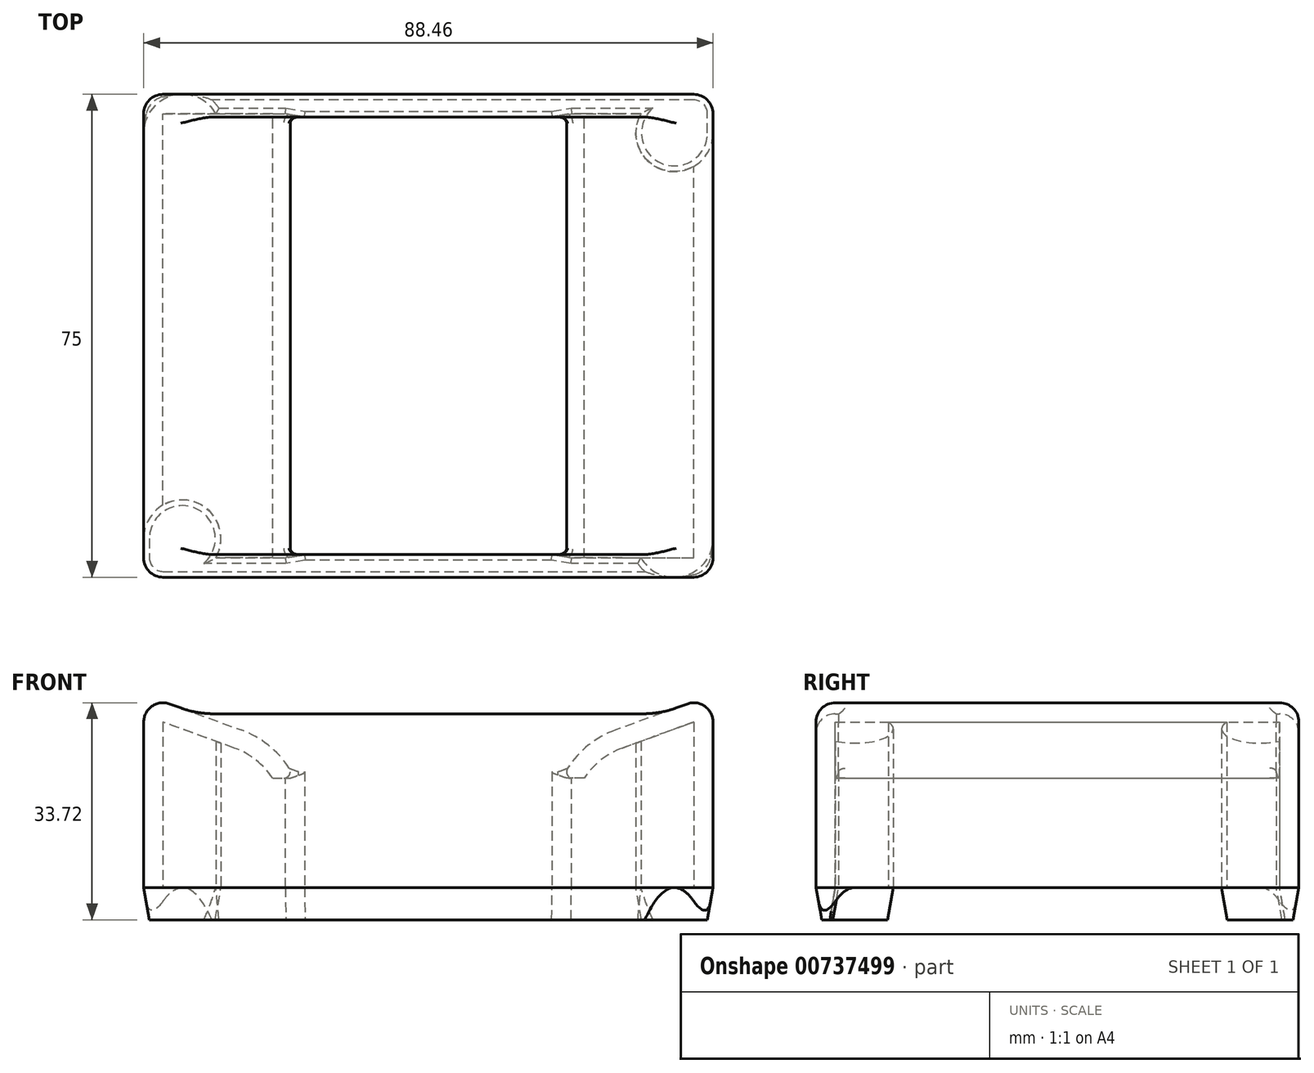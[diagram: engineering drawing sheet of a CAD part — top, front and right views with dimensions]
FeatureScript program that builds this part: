
annotation { "Feature Type Name" : "Feature", "Feature Type Description" : "" }
export const myFeature = defineFeature(function(context is Context, id is Id, definition is map)
    precondition{}
    {
        {
            var Q0;
            Q0=qCreatedBy(makeId("Front.planeOp"),FACE);
            var sketch = newSketch(context, id + "F0", { "sketchPlane" : qUnion([Q0])});
            skCircle(sketch, "E0", {"center": v(0, 115) * mm, "radius": 95 * mm, "construction": true});
            skPoint(sketch, "E1.middle", {"position": v(0, 0) * mm});
            skLineSegment(sketch, "E2", {"start": v(-44.23, 0) * mm, "end": v(44.23, 0) * mm});
            skLineSegment(sketch, "E3", {"start": v(-19.23, 20.9) * mm, "end": v(-19.23, 0) * mm});
            skLineSegment(sketch, "E4", {"start": v(-44.23, 30) * mm, "end": v(-19.23, 20.9) * mm});
            skLineSegment(sketch, "E5", {"start": v(-44.23, 30) * mm, "end": v(-44.23, 0) * mm});
            skLineSegment(sketch, "E6.MirrorCS", {"start": v(44.23, 30) * mm, "end": v(44.23, 0) * mm});
            skLineSegment(sketch, "E7.MirrorCS", {"start": v(19.23, 20.9) * mm, "end": v(19.23, 0) * mm});
            skLineSegment(sketch, "E8.MirrorCS", {"start": v(44.23, 30) * mm, "end": v(19.23, 20.9) * mm});
            skLineSegment(sketch, "E9", {"start": v(-35.98, 27) * mm, "end": v(35.98, 27) * mm});
            skSolve(sketch);
        }
        {
            var Q0;
            {var subQ3=sQuery(id+"F0.wireOp",EDGE,"E3");Q0=makeQuery(id+"F0.imprint","IMPRINT",FACE,{"disambiguationData":[TD([[makeQuery(id+"F0.imprint","IMPRINT",EDGE,{"derivedFrom":subQ3}),-1.0]])]});}
            var Q1;
            {var subQ1=sQuery(id+"F0.wireOp",EDGE,"E3");Q1=makeQuery(id+"F0.imprint","IMPRINT",FACE,{"disambiguationData":[TD([[makeQuery(id+"F0.imprint","IMPRINT",EDGE,{"derivedFrom":subQ1}),1.0]])]});}
            var Q2;
            {var subQ1=sQuery(id+"F0.wireOp",EDGE,"E6.MirrorCS");Q2=makeQuery(id+"F0.imprint","IMPRINT",FACE,{"disambiguationData":[TD([[makeQuery(id+"F0.imprint","IMPRINT",EDGE,{"derivedFrom":subQ1}),-1.0]])]});}
            extrude(context, id + "F1", {"entities" : qUnion([Q0, Q1, Q2]), "endBound" : BoundingType.SYMMETRIC, "depth" : 75 * mm, "offsetDistance" : 25 * mm});
        }
        {
            var Q0;
            {var subQ1=sQuery(id+"F0.wireOp",EDGE,"E3");Q0=makeQuery(id+"F0.imprint","IMPRINT",FACE,{"disambiguationData":[TD([[makeQuery(id+"F0.imprint","IMPRINT",EDGE,{"derivedFrom":subQ1}),1.0]])]});}
            extrude(context, id + "F2", {"entities" : qUnion([Q0]), "operationType" : NewBodyOperationType.REMOVE, "endBound" : BoundingType.SYMMETRIC, "depth" : 68 * mm, "offsetDistance" : 25 * mm});
        }
        {
            var Q0;
            Q0=makeQuery(id+"F2.boolean.opBoolean","COPY",EDGE,{"derivedFrom":makeQuery(id+"F2.opExtrude","SWEPT_EDGE",EDGE,{"disambiguationData":[OSD([sQuery(id+"F0.wireOp",EDGE,"E3"),sQuery(id+"F0.wireOp",EDGE,"E4")])]})});
            var Q1;
            Q1=makeQuery(id+"F2.boolean.opBoolean","COPY",EDGE,{"derivedFrom":makeQuery(id+"F2.opExtrude","SWEPT_EDGE",EDGE,{"disambiguationData":[OSD([sQuery(id+"F0.wireOp",EDGE,"E7.MirrorCS"),sQuery(id+"F0.wireOp",EDGE,"E8.MirrorCS")])]})});
            var Q2;
            {var subQ0=sQuery(id+"F0.wireOp",EDGE,"E9");var subQ1=sQuery(id+"F0.wireOp",EDGE,"E8.MirrorCS");var subQ2=sQuery(id+"F0.wireOp",EDGE,"E4");var subQ3=sQuery(id+"F0.wireOp",EDGE,"E2");Q2=makeQuery(id+"F2.boolean.opBoolean","SPLIT",EDGE,{"disambiguationData":[TD([makeQuery(id+"F1.opExtrude","CAP_FACE",FACE,{"disambiguationData":[OSD([subQ3,subQ2,sQuery(id+"F0.wireOp",EDGE,"E5"),sQuery(id+"F0.wireOp",EDGE,"E6.MirrorCS"),subQ1,subQ0])],"isStart":false})])],"derivedFrom":makeQuery(id+"F1.opExtrude","SWEPT_EDGE",EDGE,{"disambiguationData":[OSD([subQ1,subQ0])]})});}
            var Q3;
            {var subQ0=sQuery(id+"F0.wireOp",EDGE,"E9");var subQ1=sQuery(id+"F0.wireOp",EDGE,"E8.MirrorCS");var subQ2=sQuery(id+"F0.wireOp",EDGE,"E4");var subQ3=sQuery(id+"F0.wireOp",EDGE,"E2");Q3=makeQuery(id+"F2.boolean.opBoolean","SPLIT",EDGE,{"disambiguationData":[TD([makeQuery(id+"F1.opExtrude","CAP_FACE",FACE,{"disambiguationData":[OSD([subQ3,subQ2,sQuery(id+"F0.wireOp",EDGE,"E5"),sQuery(id+"F0.wireOp",EDGE,"E6.MirrorCS"),subQ1,subQ0])],"isStart":false})])],"derivedFrom":makeQuery(id+"F1.opExtrude","SWEPT_EDGE",EDGE,{"disambiguationData":[OSD([subQ2,subQ0])]})});}
            var Q4;
            {var subQ0=sQuery(id+"F0.wireOp",EDGE,"E9");var subQ1=sQuery(id+"F0.wireOp",EDGE,"E8.MirrorCS");var subQ2=sQuery(id+"F0.wireOp",EDGE,"E4");var subQ3=sQuery(id+"F0.wireOp",EDGE,"E2");Q4=makeQuery(id+"F2.boolean.opBoolean","SPLIT",EDGE,{"disambiguationData":[TD([makeQuery(id+"F1.opExtrude","CAP_FACE",FACE,{"disambiguationData":[OSD([subQ3,subQ2,sQuery(id+"F0.wireOp",EDGE,"E5"),sQuery(id+"F0.wireOp",EDGE,"E6.MirrorCS"),subQ1,subQ0])],"isStart":true})])],"derivedFrom":makeQuery(id+"F1.opExtrude","SWEPT_EDGE",EDGE,{"disambiguationData":[OSD([subQ2,subQ0])]})});}
            var Q5;
            {var subQ0=sQuery(id+"F0.wireOp",EDGE,"E9");var subQ1=sQuery(id+"F0.wireOp",EDGE,"E8.MirrorCS");var subQ2=sQuery(id+"F0.wireOp",EDGE,"E4");var subQ3=sQuery(id+"F0.wireOp",EDGE,"E2");Q5=makeQuery(id+"F2.boolean.opBoolean","SPLIT",EDGE,{"disambiguationData":[TD([makeQuery(id+"F1.opExtrude","CAP_FACE",FACE,{"disambiguationData":[OSD([subQ3,subQ2,sQuery(id+"F0.wireOp",EDGE,"E5"),sQuery(id+"F0.wireOp",EDGE,"E6.MirrorCS"),subQ1,subQ0])],"isStart":true})])],"derivedFrom":makeQuery(id+"F1.opExtrude","SWEPT_EDGE",EDGE,{"disambiguationData":[OSD([subQ1,subQ0])]})});}
            fillet(context, id + "F3", {"entities" : qUnion([Q0, Q1, Q2, Q3, Q4, Q5]), "radius" : 15 * mm, "tangentPropagation" : true, "allowEdgeOverflow" : false});
        }
        {
            var Q0;
            Q0=makeQuery(id+"F1.opExtrude","SWEPT_EDGE",EDGE,{"disambiguationData":[OSD([sQuery(id+"F0.wireOp",EDGE,"E4"),sQuery(id+"F0.wireOp",EDGE,"E5")])]});
            var Q1;
            Q1=makeQuery(id+"F1.opExtrude","SWEPT_EDGE",EDGE,{"disambiguationData":[OSD([sQuery(id+"F0.wireOp",EDGE,"E6.MirrorCS"),sQuery(id+"F0.wireOp",EDGE,"E8.MirrorCS")])]});
            fillet(context, id + "F4", {"entities" : qUnion([Q0, Q1]), "radius" : 3 * mm, "tangentPropagation" : true, "allowEdgeOverflow" : false});
        }
        {
            var Q0;
            Q0=makeQuery(id+"F1.opExtrude","CAP_EDGE",EDGE,{"disambiguationData":[OSD([sQuery(id+"F0.wireOp",EDGE,"E5")])],"isStart":false});
            var Q1;
            Q1=makeQuery(id+"F1.opExtrude","CAP_EDGE",EDGE,{"disambiguationData":[OSD([sQuery(id+"F0.wireOp",EDGE,"E5")])],"isStart":true});
            fillet(context, id + "F5", {"entities" : qUnion([Q0, Q1]), "radius" : 3 * mm, "tangentPropagation" : true, "allowEdgeOverflow" : false});
        }
        {
            var Q0;
            Q0=makeQuery(id+"F1.opExtrude","SWEPT_FACE",FACE,{"disambiguationData":[OSD([sQuery(id+"F0.wireOp",EDGE,"E2")])]});
            shell(context, id + "F6", {"entities" : qUnion([Q0]), "thickness" : 3 * mm});
        }
        {
            var Q0;
            Q0=makeQuery(id+"F1.opExtrude","SWEPT_FACE",FACE,{"disambiguationData":[OSD([sQuery(id+"F0.wireOp",EDGE,"E2")])]});
            var sketch = newSketch(context, id + "F7", { "sketchPlane" : qUnion([Q0])});
            skLineSegment(sketch, "E10", {"start": v(19.23, -34) * mm, "end": v(22.23, -34.5) * mm});
            skLineSegment(sketch, "E11", {"start": v(-19.23, -34) * mm, "end": v(-22.23, -34.5) * mm});
            skLineSegment(sketch, "E12", {"start": v(-19.23, 34) * mm, "end": v(-22.23, 34.5) * mm});
            skLineSegment(sketch, "E13", {"start": v(19.23, 34) * mm, "end": v(22.23, 34.5) * mm});
            skSolve(sketch);
        }
        {
            var Q0;
            Q0=makeQuery(id+"F7.imprint","IMPRINT",FACE,{"disambiguationData":[TD([[makeQuery(id+"F7.imprint","IMPRINT",EDGE,{"derivedFrom":sQuery(id+"F7.wireOp",EDGE,"E10")}),1.0]])]});
            var Q1;
            Q1=makeQuery(id+"F7.imprint","IMPRINT",FACE,{"disambiguationData":[TD([[makeQuery(id+"F7.imprint","IMPRINT",EDGE,{"derivedFrom":sQuery(id+"F7.wireOp",EDGE,"E11")}),-1.0]])]});
            extrude(context, id + "F8", {"entities" : qUnion([Q0, Q1]), "operationType" : NewBodyOperationType.REMOVE, "oppositeDirection" : true, "depth" : 17 * mm, "offsetDistance" : 25 * mm});
        }
        {
            var Q0;
            Q0=makeQuery(id+"F2.boolean.opBoolean","COPY",EDGE,{"derivedFrom":makeQuery(id+"F2.opExtrude","CAP_EDGE",EDGE,{"disambiguationData":[OSD([sQuery(id+"F0.wireOp",EDGE,"E8.MirrorCS")])],"isStart":false})});
            var Q1;
            {var subQ0=sQuery(id+"F0.wireOp",EDGE,"E4");var subQ1=sQuery(id+"F0.wireOp",EDGE,"E3");Q1=makeQuery(id+"F8.boolean.opBoolean","SPLIT",EDGE,{"derivedFrom":makeQuery(id+"F3.opFillet","BLEND_EDGE",EDGE,{"blendedFrom":[makeQuery(id+"F2.boolean.opBoolean","COPY",EDGE,{"derivedFrom":makeQuery(id+"F2.opExtrude","SWEPT_EDGE",EDGE,{"disambiguationData":[OSD([subQ1,subQ0])]})}),makeQuery(id+"F2.boolean.opBoolean","COPY",FACE,{"derivedFrom":makeQuery(id+"F2.opExtrude","CAP_FACE",FACE,{"disambiguationData":[OSD([sQuery(id+"F0.wireOp",EDGE,"E2"),subQ1,subQ0,sQuery(id+"F0.wireOp",EDGE,"E7.MirrorCS"),sQuery(id+"F0.wireOp",EDGE,"E8.MirrorCS"),sQuery(id+"F0.wireOp",EDGE,"E9")])],"isStart":false})})],"blendedInto":[makeQuery(id+"F2.boolean.opBoolean","COPY",FACE,{"derivedFrom":makeQuery(id+"F2.opExtrude","CAP_FACE",FACE,{"disambiguationData":[OSD([sQuery(id+"F0.wireOp",EDGE,"E2"),subQ1,subQ0,sQuery(id+"F0.wireOp",EDGE,"E7.MirrorCS"),sQuery(id+"F0.wireOp",EDGE,"E8.MirrorCS"),sQuery(id+"F0.wireOp",EDGE,"E9")])],"isStart":false})})]})});}
            var Q2;
            {var subQ0=sQuery(id+"F0.wireOp",EDGE,"E4");var subQ1=sQuery(id+"F0.wireOp",EDGE,"E3");Q2=makeQuery(id+"F8.boolean.opBoolean","SPLIT",EDGE,{"derivedFrom":makeQuery(id+"F3.opFillet","BLEND_EDGE",EDGE,{"blendedFrom":[makeQuery(id+"F2.boolean.opBoolean","COPY",EDGE,{"derivedFrom":makeQuery(id+"F2.opExtrude","SWEPT_EDGE",EDGE,{"disambiguationData":[OSD([subQ1,subQ0])]})}),makeQuery(id+"F2.boolean.opBoolean","COPY",FACE,{"derivedFrom":makeQuery(id+"F2.opExtrude","CAP_FACE",FACE,{"disambiguationData":[OSD([sQuery(id+"F0.wireOp",EDGE,"E2"),subQ1,subQ0,sQuery(id+"F0.wireOp",EDGE,"E7.MirrorCS"),sQuery(id+"F0.wireOp",EDGE,"E8.MirrorCS"),sQuery(id+"F0.wireOp",EDGE,"E9")])],"isStart":true})})],"blendedInto":[makeQuery(id+"F2.boolean.opBoolean","COPY",FACE,{"derivedFrom":makeQuery(id+"F2.opExtrude","CAP_FACE",FACE,{"disambiguationData":[OSD([sQuery(id+"F0.wireOp",EDGE,"E2"),subQ1,subQ0,sQuery(id+"F0.wireOp",EDGE,"E7.MirrorCS"),sQuery(id+"F0.wireOp",EDGE,"E8.MirrorCS"),sQuery(id+"F0.wireOp",EDGE,"E9")])],"isStart":true})})]})});}
            var Q3;
            {var subQ0=sQuery(id+"F0.wireOp",EDGE,"E8.MirrorCS");var subQ1=sQuery(id+"F0.wireOp",EDGE,"E7.MirrorCS");Q3=makeQuery(id+"F8.boolean.opBoolean","SPLIT",EDGE,{"derivedFrom":makeQuery(id+"F3.opFillet","BLEND_EDGE",EDGE,{"blendedFrom":[makeQuery(id+"F2.boolean.opBoolean","COPY",EDGE,{"derivedFrom":makeQuery(id+"F2.opExtrude","SWEPT_EDGE",EDGE,{"disambiguationData":[OSD([subQ1,subQ0])]})}),makeQuery(id+"F2.boolean.opBoolean","COPY",FACE,{"derivedFrom":makeQuery(id+"F2.opExtrude","CAP_FACE",FACE,{"disambiguationData":[OSD([sQuery(id+"F0.wireOp",EDGE,"E2"),sQuery(id+"F0.wireOp",EDGE,"E3"),sQuery(id+"F0.wireOp",EDGE,"E4"),subQ1,subQ0,sQuery(id+"F0.wireOp",EDGE,"E9")])],"isStart":true})})],"blendedInto":[makeQuery(id+"F2.boolean.opBoolean","COPY",FACE,{"derivedFrom":makeQuery(id+"F2.opExtrude","CAP_FACE",FACE,{"disambiguationData":[OSD([sQuery(id+"F0.wireOp",EDGE,"E2"),sQuery(id+"F0.wireOp",EDGE,"E3"),sQuery(id+"F0.wireOp",EDGE,"E4"),subQ1,subQ0,sQuery(id+"F0.wireOp",EDGE,"E9")])],"isStart":true})})]})});}
            fillet(context, id + "F9", {"entities" : qUnion([Q0, Q1, Q2, Q3]), "radius" : 1 * mm, "tangentPropagation" : true, "allowEdgeOverflow" : false});
        }
        {
            var Q0;
            {var subQ0=sQuery(id+"F0.wireOp",EDGE,"E7.MirrorCS");var subQ1=sQuery(id+"F0.wireOp",EDGE,"E2");Q0=makeQuery(id+"F8.boolean.opBoolean","COPY",FACE,{"derivedFrom":makeQuery(id+"F8.opExtrude","SWEPT_FACE",FACE,{"disambiguationData":[OSD([subQ1,subQ0]),TDD([makeQuery(id+"F7.imprint","IMPRINT",EDGE,{"derivedFrom":makeQuery(id+"F6.opShell","OFFSET_EDGE",EDGE,{"disambiguationData":[OSD([subQ1,subQ0])]})})])]})});}
            extrude(context, id + "F10", {"entities" : qUnion([Q0]), "operationType" : NewBodyOperationType.REMOVE, "oppositeDirection" : true, "depth" : 5 * mm, "offsetDistance" : 25 * mm});
        }
        {
            var Q0;
            {var subQ0=sQuery(id+"F0.wireOp",EDGE,"E3");var subQ1=sQuery(id+"F0.wireOp",EDGE,"E2");Q0=makeQuery(id+"F8.boolean.opBoolean","COPY",FACE,{"derivedFrom":makeQuery(id+"F8.opExtrude","SWEPT_FACE",FACE,{"disambiguationData":[OSD([subQ1,subQ0]),TDD([makeQuery(id+"F7.imprint","IMPRINT",EDGE,{"derivedFrom":makeQuery(id+"F6.opShell","OFFSET_EDGE",EDGE,{"disambiguationData":[OSD([subQ1,subQ0])]})})])]})});}
            extrude(context, id + "F11", {"entities" : qUnion([Q0]), "operationType" : NewBodyOperationType.REMOVE, "oppositeDirection" : true, "depth" : 5 * mm, "offsetDistance" : 25 * mm});
        }
        {
            var Q0;
            Q0=makeQuery(id+"F1.opExtrude","SWEPT_FACE",FACE,{"disambiguationData":[OSD([sQuery(id+"F0.wireOp",EDGE,"E2")])]});
            var sketch = newSketch(context, id + "F12", { "sketchPlane" : qUnion([Q0])});
            skCircle(sketch, "E14", {"center": v(-38.23, 31.5) * mm, "radius": 6 * mm});
            skCircle(sketch, "E15.MirrorC", {"center": v(38.23, 31.5) * mm, "radius": 6 * mm});
            skCircle(sketch, "E16.MirrorC", {"center": v(-38.23, -31.5) * mm, "radius": 6 * mm});
            skCircle(sketch, "E17.MirrorC", {"center": v(38.23, -31.5) * mm, "radius": 6 * mm});
            skSolve(sketch);
        }
        {
            var Q0;
            {var subQ0=sQuery(id+"F12.wireOp",EDGE,"E14");var subQ1=sQuery(id+"F0.wireOp",EDGE,"E2");var subQ2=makeQuery(id+"F6.opShell","OFFSET_EDGE",EDGE,{"disambiguationData":[OSD([subQ1]),TDD([makeQuery(id+"F1.opExtrude","CAP_EDGE",EDGE,{"disambiguationData":[OSD([subQ1])],"isStart":false})]),OD(0.0)]});var subQ3=makeQuery(id+"F12.imprint","INTERSECT",VERTEX,{"derivedFrom":[subQ2,subQ0]});Q0=makeQuery(id+"F12.imprint","IMPRINT",FACE,{"disambiguationData":[TD([[makeQuery(id+"F12.imprint","IMPRINT",EDGE,{"disambiguationData":[TD([[subQ3,1.0]])],"derivedFrom":subQ0}),1.0]])]});}
            var Q1;
            {var subQ0=sQuery(id+"F12.wireOp",EDGE,"E16.MirrorC");var subQ1=sQuery(id+"F0.wireOp",EDGE,"E2");var subQ2=makeQuery(id+"F6.opShell","OFFSET_EDGE",EDGE,{"disambiguationData":[OSD([subQ1]),TDD([makeQuery(id+"F1.opExtrude","CAP_EDGE",EDGE,{"disambiguationData":[OSD([subQ1])],"isStart":true})]),OD(0.0)]});var subQ3=makeQuery(id+"F12.imprint","INTERSECT",VERTEX,{"derivedFrom":[subQ2,subQ0]});Q1=makeQuery(id+"F12.imprint","IMPRINT",FACE,{"disambiguationData":[TD([[makeQuery(id+"F12.imprint","IMPRINT",EDGE,{"disambiguationData":[TD([[subQ3,1.0]])],"derivedFrom":subQ0}),-1.0]])]});}
            var Q2;
            Q2=makeQuery(id+"F6.opShell","OFFSET_FACE",FACE,{"disambiguationData":[OSD([sQuery(id+"F0.wireOp",EDGE,"E4")])]});
            extrude(context, id + "F13", {"entities" : qUnion([Q0, Q1]), "operationType" : NewBodyOperationType.ADD, "endBound" : BoundingType.UP_TO_SURFACE, "oppositeDirection" : true, "depth" : 25 * mm, "endBoundEntityFace" : qUnion([Q2]), "offsetDistance" : 25 * mm});
        }
        {
            var Q0;
            {var subQ0=sQuery(id+"F12.wireOp",EDGE,"E15.MirrorC");var subQ1=sQuery(id+"F0.wireOp",EDGE,"E2");var subQ2=makeQuery(id+"F6.opShell","OFFSET_EDGE",EDGE,{"disambiguationData":[OSD([subQ1]),TDD([makeQuery(id+"F1.opExtrude","CAP_EDGE",EDGE,{"disambiguationData":[OSD([subQ1])],"isStart":false})]),OD(1.0)]});var subQ3=makeQuery(id+"F12.imprint","INTERSECT",VERTEX,{"derivedFrom":[subQ2,subQ0]});Q0=makeQuery(id+"F12.imprint","IMPRINT",FACE,{"disambiguationData":[TD([[makeQuery(id+"F12.imprint","IMPRINT",EDGE,{"disambiguationData":[TD([[subQ3,1.0]])],"derivedFrom":subQ0}),-1.0]])]});}
            var Q1;
            {var subQ0=sQuery(id+"F12.wireOp",EDGE,"E17.MirrorC");var subQ1=sQuery(id+"F0.wireOp",EDGE,"E2");var subQ2=makeQuery(id+"F6.opShell","OFFSET_EDGE",EDGE,{"disambiguationData":[OSD([subQ1]),TDD([makeQuery(id+"F1.opExtrude","CAP_EDGE",EDGE,{"disambiguationData":[OSD([subQ1])],"isStart":true})]),OD(1.0)]});var subQ3=makeQuery(id+"F12.imprint","INTERSECT",VERTEX,{"derivedFrom":[subQ2,subQ0]});Q1=makeQuery(id+"F12.imprint","IMPRINT",FACE,{"disambiguationData":[TD([[makeQuery(id+"F12.imprint","IMPRINT",EDGE,{"disambiguationData":[TD([[subQ3,1.0]])],"derivedFrom":subQ0}),1.0]])]});}
            var Q2;
            Q2=makeQuery(id+"F6.opShell","OFFSET_FACE",FACE,{"disambiguationData":[OSD([sQuery(id+"F0.wireOp",EDGE,"E8.MirrorCS")])]});
            extrude(context, id + "F14", {"entities" : qUnion([Q0, Q1]), "operationType" : NewBodyOperationType.ADD, "endBound" : BoundingType.UP_TO_SURFACE, "oppositeDirection" : true, "depth" : 25 * mm, "endBoundEntityFace" : qUnion([Q2]), "offsetDistance" : 25 * mm});
        }
        {
            var Q0;
            {var subQ0=sQuery(id+"F0.wireOp",EDGE,"E7.MirrorCS");Q0=makeQuery(id+"F8.boolean.opBoolean","INTERSECT",EDGE,{"derivedFrom":[makeQuery(id+"F3.opFillet","BLEND_FACE",FACE,{"disambiguationData":[OSD([subQ0,sQuery(id+"F0.wireOp",EDGE,"E8.MirrorCS")])]}),makeQuery(id+"F8.opExtrude","CAP_FACE",FACE,{"disambiguationData":[OSD([sQuery(id+"F0.wireOp",EDGE,"E2"),subQ0,sQuery(id+"F7.wireOp",EDGE,"E10"),sQuery(id+"F7.wireOp",EDGE,"E13")])],"isStart":false})]});}
            var Q1;
            {var subQ0=sQuery(id+"F0.wireOp",EDGE,"E3");Q1=makeQuery(id+"F8.boolean.opBoolean","INTERSECT",EDGE,{"derivedFrom":[makeQuery(id+"F3.opFillet","BLEND_FACE",FACE,{"disambiguationData":[OSD([subQ0,sQuery(id+"F0.wireOp",EDGE,"E4")])]}),makeQuery(id+"F8.opExtrude","CAP_FACE",FACE,{"disambiguationData":[OSD([sQuery(id+"F0.wireOp",EDGE,"E2"),subQ0,sQuery(id+"F7.wireOp",EDGE,"E11"),sQuery(id+"F7.wireOp",EDGE,"E12")])],"isStart":false})]});}
            fillet(context, id + "F15", {"entities" : qUnion([Q0, Q1]), "radius" : 1 * mm, "tangentPropagation" : true, "allowEdgeOverflow" : false});
        }
        {
            var Q0;
            {var subQ0=sQuery(id+"F0.wireOp",EDGE,"E2");var subQ1=makeQuery(id+"F1.opExtrude","CAP_EDGE",EDGE,{"disambiguationData":[OSD([subQ0])],"isStart":true});var subQ6=sQuery(id+"F12.wireOp",EDGE,"E17.MirrorC");var subQ9=makeQuery(id+"F12.imprint","INTERSECT",VERTEX,{"derivedFrom":[subQ1,subQ6]});Q0=makeQuery(id+"F12.imprint","IMPRINT",FACE,{"disambiguationData":[TD([[makeQuery(id+"F12.imprint","IMPRINT",EDGE,{"disambiguationData":[TD([[subQ9,1.0]])],"derivedFrom":subQ6}),1.0]])]});}
            var Q1;
            {var subQ0=sQuery(id+"F12.wireOp",EDGE,"E17.MirrorC");var subQ1=sQuery(id+"F0.wireOp",EDGE,"E2");var subQ2=makeQuery(id+"F6.opShell","OFFSET_EDGE",EDGE,{"disambiguationData":[OSD([subQ1]),TDD([makeQuery(id+"F1.opExtrude","CAP_EDGE",EDGE,{"disambiguationData":[OSD([subQ1])],"isStart":true})]),OD(1.0)]});var subQ3=makeQuery(id+"F12.imprint","INTERSECT",VERTEX,{"derivedFrom":[subQ2,subQ0]});Q1=makeQuery(id+"F12.imprint","IMPRINT",FACE,{"disambiguationData":[TD([[makeQuery(id+"F12.imprint","IMPRINT",EDGE,{"disambiguationData":[TD([[subQ3,1.0]])],"derivedFrom":subQ0}),1.0]])]});}
            var Q2;
            {var subQ0=sQuery(id+"F12.wireOp",EDGE,"E15.MirrorC");var subQ1=sQuery(id+"F0.wireOp",EDGE,"E2");var subQ2=makeQuery(id+"F6.opShell","OFFSET_EDGE",EDGE,{"disambiguationData":[OSD([subQ1]),TDD([makeQuery(id+"F1.opExtrude","CAP_EDGE",EDGE,{"disambiguationData":[OSD([subQ1])],"isStart":false})]),OD(1.0)]});var subQ3=makeQuery(id+"F12.imprint","INTERSECT",VERTEX,{"derivedFrom":[subQ2,subQ0]});Q2=makeQuery(id+"F12.imprint","IMPRINT",FACE,{"disambiguationData":[TD([[makeQuery(id+"F12.imprint","IMPRINT",EDGE,{"disambiguationData":[TD([[subQ3,1.0]])],"derivedFrom":subQ0}),-1.0]])]});}
            var Q3;
            {var subQ0=sQuery(id+"F0.wireOp",EDGE,"E2");var subQ1=makeQuery(id+"F1.opExtrude","CAP_EDGE",EDGE,{"disambiguationData":[OSD([subQ0])],"isStart":false});var subQ6=sQuery(id+"F12.wireOp",EDGE,"E15.MirrorC");var subQ10=makeQuery(id+"F12.imprint","INTERSECT",VERTEX,{"derivedFrom":[subQ1,subQ6]});Q3=makeQuery(id+"F12.imprint","IMPRINT",FACE,{"disambiguationData":[TD([[makeQuery(id+"F12.imprint","IMPRINT",EDGE,{"disambiguationData":[TD([[subQ10,1.0]])],"derivedFrom":subQ6}),-1.0]])]});}
            var Q4;
            {var subQ1=sQuery(id+"F0.wireOp",EDGE,"E2");var subQ4=sQuery(id+"F0.wireOp",EDGE,"E6.MirrorCS");var subQ7=makeQuery(id+"F5.opFillet","BLEND_EDGE",EDGE,{"blendedFrom":[makeQuery(id+"F1.opExtrude","CAP_EDGE",EDGE,{"disambiguationData":[OSD([subQ4])],"isStart":false}),makeQuery(id+"F1.opExtrude","SWEPT_FACE",FACE,{"disambiguationData":[OSD([subQ1])]})],"blendedInto":[makeQuery(id+"F1.opExtrude","SWEPT_FACE",FACE,{"disambiguationData":[OSD([subQ1])]})]});Q4=makeQuery(id+"F12.imprint","IMPRINT",FACE,{"disambiguationData":[TD([[makeQuery(id+"F12.imprint","IMPRINT",EDGE,{"derivedFrom":subQ7}),1.0]])]});}
            var Q5;
            {var subQ1=sQuery(id+"F0.wireOp",EDGE,"E2");var subQ4=sQuery(id+"F0.wireOp",EDGE,"E6.MirrorCS");var subQ7=makeQuery(id+"F5.opFillet","BLEND_EDGE",EDGE,{"blendedFrom":[makeQuery(id+"F1.opExtrude","CAP_EDGE",EDGE,{"disambiguationData":[OSD([subQ4])],"isStart":true}),makeQuery(id+"F1.opExtrude","SWEPT_FACE",FACE,{"disambiguationData":[OSD([subQ1])]})],"blendedInto":[makeQuery(id+"F1.opExtrude","SWEPT_FACE",FACE,{"disambiguationData":[OSD([subQ1])]})]});Q5=makeQuery(id+"F12.imprint","IMPRINT",FACE,{"disambiguationData":[TD([[makeQuery(id+"F12.imprint","IMPRINT",EDGE,{"derivedFrom":subQ7}),1.0]])]});}
            var Q6;
            {var subQ0=sQuery(id+"F12.wireOp",EDGE,"E16.MirrorC");var subQ1=sQuery(id+"F0.wireOp",EDGE,"E2");var subQ2=makeQuery(id+"F6.opShell","OFFSET_EDGE",EDGE,{"disambiguationData":[OSD([subQ1]),TDD([makeQuery(id+"F1.opExtrude","CAP_EDGE",EDGE,{"disambiguationData":[OSD([subQ1])],"isStart":true})]),OD(0.0)]});var subQ3=makeQuery(id+"F12.imprint","INTERSECT",VERTEX,{"derivedFrom":[subQ2,subQ0]});Q6=makeQuery(id+"F12.imprint","IMPRINT",FACE,{"disambiguationData":[TD([[makeQuery(id+"F12.imprint","IMPRINT",EDGE,{"disambiguationData":[TD([[subQ3,1.0]])],"derivedFrom":subQ0}),-1.0]])]});}
            var Q7;
            {var subQ1=sQuery(id+"F0.wireOp",EDGE,"E2");var subQ4=sQuery(id+"F0.wireOp",EDGE,"E5");var subQ7=makeQuery(id+"F5.opFillet","BLEND_EDGE",EDGE,{"blendedFrom":[makeQuery(id+"F1.opExtrude","CAP_EDGE",EDGE,{"disambiguationData":[OSD([subQ4])],"isStart":true}),makeQuery(id+"F1.opExtrude","SWEPT_FACE",FACE,{"disambiguationData":[OSD([subQ1])]})],"blendedInto":[makeQuery(id+"F1.opExtrude","SWEPT_FACE",FACE,{"disambiguationData":[OSD([subQ1])]})]});Q7=makeQuery(id+"F12.imprint","IMPRINT",FACE,{"disambiguationData":[TD([[makeQuery(id+"F12.imprint","IMPRINT",EDGE,{"derivedFrom":subQ7}),1.0]])]});}
            var Q8;
            {var subQ0=sQuery(id+"F12.wireOp",EDGE,"E16.MirrorC");var subQ2=sQuery(id+"F0.wireOp",EDGE,"E2");var subQ6=makeQuery(id+"F1.opExtrude","CAP_EDGE",EDGE,{"disambiguationData":[OSD([subQ2])],"isStart":true});var subQ7=makeQuery(id+"F12.imprint","INTERSECT",VERTEX,{"derivedFrom":[subQ6,subQ0]});Q8=makeQuery(id+"F12.imprint","IMPRINT",FACE,{"disambiguationData":[TD([[makeQuery(id+"F12.imprint","IMPRINT",EDGE,{"disambiguationData":[TD([[subQ7,1.0]])],"derivedFrom":subQ0}),-1.0]])]});}
            var Q9;
            {var subQ0=sQuery(id+"F12.wireOp",EDGE,"E14");var subQ1=sQuery(id+"F0.wireOp",EDGE,"E2");var subQ2=makeQuery(id+"F6.opShell","OFFSET_EDGE",EDGE,{"disambiguationData":[OSD([subQ1]),TDD([makeQuery(id+"F1.opExtrude","CAP_EDGE",EDGE,{"disambiguationData":[OSD([subQ1])],"isStart":false})]),OD(0.0)]});var subQ3=makeQuery(id+"F12.imprint","INTERSECT",VERTEX,{"derivedFrom":[subQ2,subQ0]});Q9=makeQuery(id+"F12.imprint","IMPRINT",FACE,{"disambiguationData":[TD([[makeQuery(id+"F12.imprint","IMPRINT",EDGE,{"disambiguationData":[TD([[subQ3,1.0]])],"derivedFrom":subQ0}),1.0]])]});}
            var Q10;
            {var subQ0=sQuery(id+"F0.wireOp",EDGE,"E2");var subQ1=makeQuery(id+"F1.opExtrude","CAP_EDGE",EDGE,{"disambiguationData":[OSD([subQ0])],"isStart":false});var subQ6=sQuery(id+"F12.wireOp",EDGE,"E14");var subQ9=makeQuery(id+"F12.imprint","INTERSECT",VERTEX,{"derivedFrom":[subQ1,subQ6]});Q10=makeQuery(id+"F12.imprint","IMPRINT",FACE,{"disambiguationData":[TD([[makeQuery(id+"F12.imprint","IMPRINT",EDGE,{"disambiguationData":[TD([[subQ9,1.0]])],"derivedFrom":subQ6}),1.0]])]});}
            var Q11;
            {var subQ1=sQuery(id+"F0.wireOp",EDGE,"E2");var subQ4=sQuery(id+"F0.wireOp",EDGE,"E5");var subQ7=makeQuery(id+"F5.opFillet","BLEND_EDGE",EDGE,{"blendedFrom":[makeQuery(id+"F1.opExtrude","CAP_EDGE",EDGE,{"disambiguationData":[OSD([subQ4])],"isStart":false}),makeQuery(id+"F1.opExtrude","SWEPT_FACE",FACE,{"disambiguationData":[OSD([subQ1])]})],"blendedInto":[makeQuery(id+"F1.opExtrude","SWEPT_FACE",FACE,{"disambiguationData":[OSD([subQ1])]})]});Q11=makeQuery(id+"F12.imprint","IMPRINT",FACE,{"disambiguationData":[TD([[makeQuery(id+"F12.imprint","IMPRINT",EDGE,{"derivedFrom":subQ7}),1.0]])]});}
            extrude(context, id + "F16", {"entities" : qUnion([Q0, Q1, Q2, Q3, Q4, Q5, Q6, Q7, Q8, Q9, Q10, Q11]), "operationType" : NewBodyOperationType.ADD, "depth" : 5 * mm, "offsetDistance" : 25 * mm, "hasDraft" : true, "draftAngle" : 10 * degree, "draftPullDirection" : true});
        }
    });
